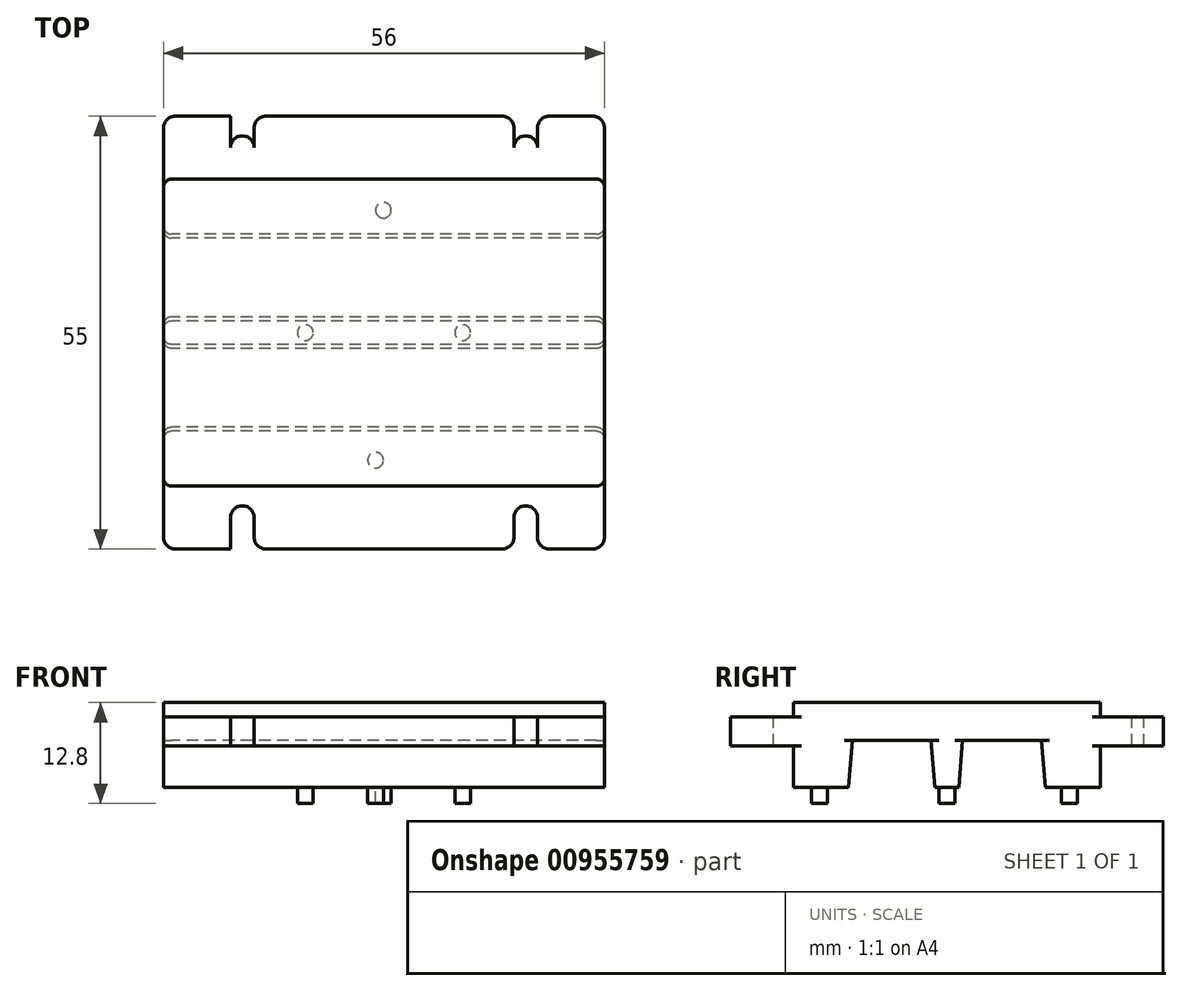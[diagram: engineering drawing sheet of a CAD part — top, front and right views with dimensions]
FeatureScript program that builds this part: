
annotation { "Feature Type Name" : "Feature", "Feature Type Description" : "" }
export const myFeature = defineFeature(function(context is Context, id is Id, definition is map)
    precondition{}
    {
        {
            var Q0;
            Q0=qCreatedBy(makeId("Right.planeOp"),FACE);
            var sketch = newSketch(context, id + "F0", { "sketchPlane" : qUnion([Q0])});
            skLineSegment(sketch, "E0.bottom", {"start": v(0, 0) * mm, "end": v(19.5, 0) * mm});
            skLineSegment(sketch, "E0.top", {"start": v(0, 9) * mm, "end": v(19.5, 9) * mm});
            skLineSegment(sketch, "E0.left", {"start": v(0, 0) * mm, "end": v(0, 9) * mm});
            skLineSegment(sketch, "E0.right", {"start": v(19.5, 0) * mm, "end": v(19.5, 9) * mm});
            skLineSegment(sketch, "E1.bottom", {"start": v(0, 0) * mm, "end": v(-19.5, 0) * mm});
            skLineSegment(sketch, "E1.top", {"start": v(0, 9) * mm, "end": v(-19.5, 9) * mm});
            skLineSegment(sketch, "E1.right", {"start": v(-19.5, 0) * mm, "end": v(-19.5, 9) * mm});
            skLineSegment(sketch, "E2.bottom", {"start": v(19.5, 9) * mm, "end": v(27.5, 9) * mm});
            skLineSegment(sketch, "E2.top", {"start": v(19.5, 5.3) * mm, "end": v(27.5, 5.3) * mm});
            skLineSegment(sketch, "E2.left", {"start": v(19.5, 9) * mm, "end": v(19.5, 5.3) * mm});
            skLineSegment(sketch, "E2.right", {"start": v(27.5, 9) * mm, "end": v(27.5, 5.3) * mm});
            skLineSegment(sketch, "E3.bottom", {"start": v(-19.5, 9) * mm, "end": v(-27.5, 9) * mm});
            skLineSegment(sketch, "E3.top", {"start": v(-19.5, 5.3) * mm, "end": v(-27.5, 5.3) * mm});
            skLineSegment(sketch, "E3.left", {"start": v(-19.5, 9) * mm, "end": v(-19.5, 5.3) * mm});
            skLineSegment(sketch, "E3.right", {"start": v(-27.5, 9) * mm, "end": v(-27.5, 5.3) * mm});
            skLineSegment(sketch, "E4", {"start": v(0, 0) * mm, "end": v(1.5, 0) * mm});
            skLineSegment(sketch, "E5", {"start": v(1.5, 0) * mm, "end": v(2, 6) * mm});
            skLineSegment(sketch, "E6", {"start": v(2, 6) * mm, "end": v(12, 6) * mm});
            skLineSegment(sketch, "E7", {"start": v(12, 6) * mm, "end": v(12.5, 0) * mm});
            skLineSegment(sketch, "E8.MirrorCS", {"start": v(-1.5, 0) * mm, "end": v(-2, 6) * mm});
            skLineSegment(sketch, "E9.MirrorCS", {"start": v(-2, 6) * mm, "end": v(-12, 6) * mm});
            skLineSegment(sketch, "E10.MirrorCS", {"start": v(-12, 6) * mm, "end": v(-12.5, 0) * mm});
            skSolve(sketch);
        }
        {
            var Q0;
            Q0=makeQuery(id+"F0.imprint","IMPRINT",FACE,{"disambiguationData":[TD([[makeQuery(id+"F0.imprint","IMPRINT",EDGE,{"derivedFrom":sQuery(id+"F0.wireOp",EDGE,"E1.top")}),1.0]])]});
            var Q1;
            Q1=makeQuery(id+"F0.imprint","IMPRINT",FACE,{"disambiguationData":[TD([[makeQuery(id+"F0.imprint","IMPRINT",EDGE,{"derivedFrom":sQuery(id+"F0.wireOp",EDGE,"E3.bottom")}),1.0]])]});
            var Q2;
            Q2=makeQuery(id+"F0.imprint","IMPRINT",FACE,{"disambiguationData":[TD([[makeQuery(id+"F0.imprint","IMPRINT",EDGE,{"derivedFrom":sQuery(id+"F0.wireOp",EDGE,"E0.top")}),-1.0]])]});
            var Q3;
            Q3=makeQuery(id+"F0.imprint","IMPRINT",FACE,{"disambiguationData":[TD([[makeQuery(id+"F0.imprint","IMPRINT",EDGE,{"derivedFrom":sQuery(id+"F0.wireOp",EDGE,"E2.bottom")}),-1.0]])]});
            extrude(context, id + "F1", {"entities" : qUnion([Q0, Q1, Q2, Q3]), "depth" : 56 * mm, "offsetDistance" : 25 * mm});
        }
        {
            var Q0;
            Q0=makeQuery(id+"F1.opExtrude","SWEPT_FACE",FACE,{"disambiguationData":[OSD([sQuery(id+"F0.wireOp",EDGE,"E0.top"),sQuery(id+"F0.wireOp",EDGE,"E1.top"),sQuery(id+"F0.wireOp",EDGE,"E2.bottom"),sQuery(id+"F0.wireOp",EDGE,"E3.bottom")])]});
            var sketch = newSketch(context, id + "F2", { "sketchPlane" : qUnion([Q0])});
            skPoint(sketch, "E11", {"position": v(10, 23.5) * mm});
            skPoint(sketch, "E12", {"position": v(46, 23.5) * mm});
            skPoint(sketch, "E13", {"position": v(46, -23.5) * mm});
            skPoint(sketch, "E14", {"position": v(10, -23.5) * mm});
            skCircle(sketch, "E15", {"center": v(10, -23.5) * mm, "radius": 1.5 * mm});
            skCircle(sketch, "E16", {"center": v(46, -23.5) * mm, "radius": 1.5 * mm});
            skLineSegment(sketch, "E17", {"start": v(11.5, -23.5) * mm, "end": v(11.5, -27.5) * mm});
            skLineSegment(sketch, "E18", {"start": v(8.5, -23.5) * mm, "end": v(8.5, -27.5) * mm});
            skLineSegment(sketch, "E19", {"start": v(47.5, -23.5) * mm, "end": v(47.5, -27.5) * mm});
            skLineSegment(sketch, "E20", {"start": v(44.5, -23.5) * mm, "end": v(44.5, -27.5) * mm});
            skLineSegment(sketch, "E21", {"start": v(0, 0) * mm, "end": v(56, 0) * mm});
            skLineSegment(sketch, "E22.MirrorCS", {"start": v(8.5, 23.5) * mm, "end": v(8.5, 27.5) * mm});
            skCircle(sketch, "E23.MirrorC", {"center": v(10, 23.5) * mm, "radius": 1.5 * mm});
            skLineSegment(sketch, "E24.MirrorCS", {"start": v(11.5, 23.5) * mm, "end": v(11.5, 27.5) * mm});
            skCircle(sketch, "E25.MirrorC", {"center": v(46, 23.5) * mm, "radius": 1.5 * mm});
            skLineSegment(sketch, "E26.MirrorCS", {"start": v(44.5, 23.5) * mm, "end": v(44.5, 27.5) * mm});
            skLineSegment(sketch, "E27.MirrorCS", {"start": v(47.5, 23.5) * mm, "end": v(47.5, 27.5) * mm});
            skSolve(sketch);
        }
        {
            var Q0;
            Q0=makeQuery(id+"F1.opExtrude","SWEPT_FACE",FACE,{"disambiguationData":[OSD([sQuery(id+"F0.wireOp",EDGE,"E0.top"),sQuery(id+"F0.wireOp",EDGE,"E1.top"),sQuery(id+"F0.wireOp",EDGE,"E2.bottom"),sQuery(id+"F0.wireOp",EDGE,"E3.bottom")])]});
            var sketch = newSketch(context, id + "F3", { "sketchPlane" : qUnion([Q0])});
            skLineSegment(sketch, "E28.bottom", {"start": v(0, 19.5) * mm, "end": v(56, 19.5) * mm});
            skLineSegment(sketch, "E28.top", {"start": v(0, -19.5) * mm, "end": v(56, -19.5) * mm});
            skLineSegment(sketch, "E28.left", {"start": v(0, 19.5) * mm, "end": v(0, -19.5) * mm});
            skLineSegment(sketch, "E28.right", {"start": v(56, 19.5) * mm, "end": v(56, -19.5) * mm});
            skSolve(sketch);
        }
        {
            var Q0;
            Q0=makeQuery(id+"F3.imprint","IMPRINT",FACE,{"disambiguationData":[TD([[makeQuery(id+"F3.imprint","IMPRINT",EDGE,{"derivedFrom":sQuery(id+"F3.wireOp",EDGE,"E28.bottom")}),-1.0]])]});
            extrude(context, id + "F4", {"entities" : qUnion([Q0]), "operationType" : NewBodyOperationType.ADD, "depth" : 1.8 * mm, "offsetDistance" : 25 * mm});
        }
        {
            var Q0;
            {var subQ0=sQuery(id+"F2.wireOp",EDGE,"E17");Q0=makeQuery(id+"F2.imprint","IMPRINT",FACE,{"disambiguationData":[TD([[makeQuery(id+"F2.imprint","IMPRINT",EDGE,{"derivedFrom":subQ0}),-1.0]])]});}
            var Q1;
            {var subQ0=sQuery(id+"F2.wireOp",EDGE,"E15");var subQ1=makeQuery(id+"F2.imprint","INTERSECT",VERTEX,{"derivedFrom":[subQ0,sQuery(id+"F2.wireOp",EDGE,"E17")]});Q1=makeQuery(id+"F2.imprint","IMPRINT",FACE,{"disambiguationData":[TD([[makeQuery(id+"F2.imprint","IMPRINT",EDGE,{"disambiguationData":[TD([[subQ1,-1.0]])],"derivedFrom":subQ0}),1.0]])]});}
            var Q2;
            {var subQ0=sQuery(id+"F2.wireOp",EDGE,"E19");Q2=makeQuery(id+"F2.imprint","IMPRINT",FACE,{"disambiguationData":[TD([[makeQuery(id+"F2.imprint","IMPRINT",EDGE,{"derivedFrom":subQ0}),-1.0]])]});}
            var Q3;
            {var subQ0=sQuery(id+"F2.wireOp",EDGE,"E16");var subQ1=makeQuery(id+"F2.imprint","INTERSECT",VERTEX,{"derivedFrom":[subQ0,sQuery(id+"F2.wireOp",EDGE,"E19")]});Q3=makeQuery(id+"F2.imprint","IMPRINT",FACE,{"disambiguationData":[TD([[makeQuery(id+"F2.imprint","IMPRINT",EDGE,{"disambiguationData":[TD([[subQ1,-1.0]])],"derivedFrom":subQ0}),1.0]])]});}
            var Q4;
            {var subQ0=sQuery(id+"F2.wireOp",EDGE,"E22.MirrorCS");Q4=makeQuery(id+"F2.imprint","IMPRINT",FACE,{"disambiguationData":[TD([[makeQuery(id+"F2.imprint","IMPRINT",EDGE,{"derivedFrom":subQ0}),-1.0]])]});}
            var Q5;
            {var subQ0=sQuery(id+"F2.wireOp",EDGE,"E23.MirrorC");var subQ1=makeQuery(id+"F2.imprint","INTERSECT",VERTEX,{"derivedFrom":[sQuery(id+"F2.wireOp",EDGE,"E22.MirrorCS"),subQ0]});Q5=makeQuery(id+"F2.imprint","IMPRINT",FACE,{"disambiguationData":[TD([[makeQuery(id+"F2.imprint","IMPRINT",EDGE,{"disambiguationData":[TD([[subQ1,1.0]])],"derivedFrom":subQ0}),-1.0]])]});}
            var Q6;
            {var subQ0=sQuery(id+"F2.wireOp",EDGE,"E25.MirrorC");var subQ1=makeQuery(id+"F2.imprint","INTERSECT",VERTEX,{"derivedFrom":[subQ0,sQuery(id+"F2.wireOp",EDGE,"E26.MirrorCS")]});Q6=makeQuery(id+"F2.imprint","IMPRINT",FACE,{"disambiguationData":[TD([[makeQuery(id+"F2.imprint","IMPRINT",EDGE,{"disambiguationData":[TD([[subQ1,1.0]])],"derivedFrom":subQ0}),-1.0]])]});}
            var Q7;
            {var subQ0=sQuery(id+"F2.wireOp",EDGE,"E26.MirrorCS");Q7=makeQuery(id+"F2.imprint","IMPRINT",FACE,{"disambiguationData":[TD([[makeQuery(id+"F2.imprint","IMPRINT",EDGE,{"derivedFrom":subQ0}),-1.0]])]});}
            extrude(context, id + "F5", {"entities" : qUnion([Q0, Q1, Q2, Q3, Q4, Q5, Q6, Q7]), "operationType" : NewBodyOperationType.REMOVE, "oppositeDirection" : true, "depth" : 25 * mm, "offsetDistance" : 25 * mm});
        }
        {
            var Q0;
            Q0=makeQuery(id+"F1.opExtrude","CAP_EDGE",EDGE,{"disambiguationData":[OSD([sQuery(id+"F0.wireOp",EDGE,"E0.right")])],"isStart":false});
            var Q1;
            Q1=makeQuery(id+"F1.opExtrude","CAP_EDGE",EDGE,{"disambiguationData":[OSD([sQuery(id+"F0.wireOp",EDGE,"E7")])],"isStart":false});
            var Q2;
            Q2=makeQuery(id+"F1.opExtrude","CAP_EDGE",EDGE,{"disambiguationData":[OSD([sQuery(id+"F0.wireOp",EDGE,"E5")])],"isStart":false});
            var Q3;
            Q3=makeQuery(id+"F1.opExtrude","CAP_EDGE",EDGE,{"disambiguationData":[OSD([sQuery(id+"F0.wireOp",EDGE,"E8.MirrorCS")])],"isStart":false});
            var Q4;
            Q4=makeQuery(id+"F1.opExtrude","CAP_EDGE",EDGE,{"disambiguationData":[OSD([sQuery(id+"F0.wireOp",EDGE,"E10.MirrorCS")])],"isStart":false});
            var Q5;
            Q5=makeQuery(id+"F1.opExtrude","CAP_EDGE",EDGE,{"disambiguationData":[OSD([sQuery(id+"F0.wireOp",EDGE,"E1.right")])],"isStart":false});
            var Q6;
            Q6=makeQuery(id+"F4.opExtrude","SWEPT_EDGE",EDGE,{"disambiguationData":[OSD([sQuery(id+"F0.wireOp",EDGE,"E0.top"),sQuery(id+"F0.wireOp",EDGE,"E1.top"),sQuery(id+"F0.wireOp",EDGE,"E2.bottom"),sQuery(id+"F0.wireOp",EDGE,"E3.bottom"),sQuery(id+"F3.wireOp",EDGE,"E28.bottom"),sQuery(id+"F3.wireOp",EDGE,"E28.right")])]});
            var Q7;
            Q7=makeQuery(id+"F4.opExtrude","SWEPT_EDGE",EDGE,{"disambiguationData":[OSD([sQuery(id+"F0.wireOp",EDGE,"E0.top"),sQuery(id+"F0.wireOp",EDGE,"E1.top"),sQuery(id+"F0.wireOp",EDGE,"E2.bottom"),sQuery(id+"F0.wireOp",EDGE,"E3.bottom"),sQuery(id+"F3.wireOp",EDGE,"E28.top"),sQuery(id+"F3.wireOp",EDGE,"E28.right")])]});
            var Q8;
            Q8=makeQuery(id+"F1.opExtrude","CAP_EDGE",EDGE,{"disambiguationData":[OSD([sQuery(id+"F0.wireOp",EDGE,"E0.right")])],"isStart":true});
            var Q9;
            Q9=makeQuery(id+"F1.opExtrude","CAP_EDGE",EDGE,{"disambiguationData":[OSD([sQuery(id+"F0.wireOp",EDGE,"E7")])],"isStart":true});
            var Q10;
            Q10=makeQuery(id+"F1.opExtrude","CAP_EDGE",EDGE,{"disambiguationData":[OSD([sQuery(id+"F0.wireOp",EDGE,"E5")])],"isStart":true});
            var Q11;
            Q11=makeQuery(id+"F1.opExtrude","CAP_EDGE",EDGE,{"disambiguationData":[OSD([sQuery(id+"F0.wireOp",EDGE,"E8.MirrorCS")])],"isStart":true});
            var Q12;
            Q12=makeQuery(id+"F4.opExtrude","SWEPT_EDGE",EDGE,{"disambiguationData":[OSD([sQuery(id+"F0.wireOp",EDGE,"E0.top"),sQuery(id+"F0.wireOp",EDGE,"E1.top"),sQuery(id+"F0.wireOp",EDGE,"E2.bottom"),sQuery(id+"F0.wireOp",EDGE,"E3.bottom"),sQuery(id+"F3.wireOp",EDGE,"E28.bottom"),sQuery(id+"F3.wireOp",EDGE,"E28.left")])]});
            var Q13;
            Q13=makeQuery(id+"F1.opExtrude","CAP_EDGE",EDGE,{"disambiguationData":[OSD([sQuery(id+"F0.wireOp",EDGE,"E10.MirrorCS")])],"isStart":true});
            var Q14;
            Q14=makeQuery(id+"F1.opExtrude","CAP_EDGE",EDGE,{"disambiguationData":[OSD([sQuery(id+"F0.wireOp",EDGE,"E1.right")])],"isStart":true});
            var Q15;
            Q15=makeQuery(id+"F4.opExtrude","SWEPT_EDGE",EDGE,{"disambiguationData":[OSD([sQuery(id+"F0.wireOp",EDGE,"E0.top"),sQuery(id+"F0.wireOp",EDGE,"E1.top"),sQuery(id+"F0.wireOp",EDGE,"E2.bottom"),sQuery(id+"F0.wireOp",EDGE,"E3.bottom"),sQuery(id+"F3.wireOp",EDGE,"E28.top"),sQuery(id+"F3.wireOp",EDGE,"E28.left")])]});
            fillet(context, id + "F6", {"entities" : qUnion([Q0, Q1, Q2, Q3, Q4, Q5, Q6, Q7, Q8, Q9, Q10, Q11, Q12, Q13, Q14, Q15]), "radius" : 1 * mm, "tangentPropagation" : true, "allowEdgeOverflow" : false});
        }
        {
            var Q0;
            Q0=makeQuery(id+"F1.opExtrude","CAP_EDGE",EDGE,{"disambiguationData":[OSD([sQuery(id+"F0.wireOp",EDGE,"E3.right")])],"isStart":true});
            var Q1;
            Q1=makeQuery(id+"F5.boolean.opBoolean","COPY",EDGE,{"derivedFrom":makeQuery(id+"F5.opExtrude","SWEPT_EDGE",EDGE,{"disambiguationData":[OSD([sQuery(id+"F0.wireOp",EDGE,"E3.bottom"),sQuery(id+"F0.wireOp",EDGE,"E3.right"),sQuery(id+"F2.wireOp",EDGE,"E18")])]})});
            var Q2;
            Q2=makeQuery(id+"F5.boolean.opBoolean","COPY",EDGE,{"derivedFrom":makeQuery(id+"F5.opExtrude","SWEPT_EDGE",EDGE,{"disambiguationData":[OSD([sQuery(id+"F0.wireOp",EDGE,"E3.bottom"),sQuery(id+"F0.wireOp",EDGE,"E3.right"),sQuery(id+"F2.wireOp",EDGE,"E17")])]})});
            var Q3;
            Q3=makeQuery(id+"F5.boolean.opBoolean","COPY",EDGE,{"derivedFrom":makeQuery(id+"F5.opExtrude","SWEPT_EDGE",EDGE,{"disambiguationData":[OSD([sQuery(id+"F0.wireOp",EDGE,"E3.bottom"),sQuery(id+"F0.wireOp",EDGE,"E3.right"),sQuery(id+"F2.wireOp",EDGE,"E19")])]})});
            var Q4;
            Q4=makeQuery(id+"F5.boolean.opBoolean","COPY",EDGE,{"derivedFrom":makeQuery(id+"F5.opExtrude","SWEPT_EDGE",EDGE,{"disambiguationData":[OSD([sQuery(id+"F0.wireOp",EDGE,"E3.bottom"),sQuery(id+"F0.wireOp",EDGE,"E3.right"),sQuery(id+"F2.wireOp",EDGE,"E20")])]})});
            var Q5;
            Q5=makeQuery(id+"F1.opExtrude","CAP_EDGE",EDGE,{"disambiguationData":[OSD([sQuery(id+"F0.wireOp",EDGE,"E3.right")])],"isStart":false});
            var Q6;
            Q6=makeQuery(id+"F1.opExtrude","CAP_EDGE",EDGE,{"disambiguationData":[OSD([sQuery(id+"F0.wireOp",EDGE,"E2.right")])],"isStart":true});
            var Q7;
            Q7=makeQuery(id+"F5.boolean.opBoolean","COPY",EDGE,{"derivedFrom":makeQuery(id+"F5.opExtrude","SWEPT_EDGE",EDGE,{"disambiguationData":[OSD([sQuery(id+"F0.wireOp",EDGE,"E2.bottom"),sQuery(id+"F0.wireOp",EDGE,"E2.right"),sQuery(id+"F2.wireOp",EDGE,"E22.MirrorCS")])]})});
            var Q8;
            Q8=makeQuery(id+"F5.boolean.opBoolean","COPY",EDGE,{"derivedFrom":makeQuery(id+"F5.opExtrude","SWEPT_EDGE",EDGE,{"disambiguationData":[OSD([sQuery(id+"F0.wireOp",EDGE,"E2.bottom"),sQuery(id+"F0.wireOp",EDGE,"E2.right"),sQuery(id+"F2.wireOp",EDGE,"E24.MirrorCS")])]})});
            var Q9;
            Q9=makeQuery(id+"F5.boolean.opBoolean","COPY",EDGE,{"derivedFrom":makeQuery(id+"F5.opExtrude","SWEPT_EDGE",EDGE,{"disambiguationData":[OSD([sQuery(id+"F0.wireOp",EDGE,"E2.bottom"),sQuery(id+"F0.wireOp",EDGE,"E2.right"),sQuery(id+"F2.wireOp",EDGE,"E26.MirrorCS")])]})});
            var Q10;
            Q10=makeQuery(id+"F5.boolean.opBoolean","COPY",EDGE,{"derivedFrom":makeQuery(id+"F5.opExtrude","SWEPT_EDGE",EDGE,{"disambiguationData":[OSD([sQuery(id+"F0.wireOp",EDGE,"E2.bottom"),sQuery(id+"F0.wireOp",EDGE,"E2.right"),sQuery(id+"F2.wireOp",EDGE,"E27.MirrorCS")])]})});
            var Q11;
            Q11=makeQuery(id+"F1.opExtrude","CAP_EDGE",EDGE,{"disambiguationData":[OSD([sQuery(id+"F0.wireOp",EDGE,"E2.right")])],"isStart":false});
            fillet(context, id + "F7", {"entities" : qUnion([Q0, Q1, Q2, Q3, Q4, Q5, Q6, Q7, Q8, Q9, Q10, Q11]), "radius" : 1.5 * mm, "tangentPropagation" : true, "allowEdgeOverflow" : false});
        }
        {
            var Q0;
            Q0=makeQuery(id+"F1.opExtrude","SWEPT_FACE",FACE,{"disambiguationData":[OSD([sQuery(id+"F0.wireOp",EDGE,"E1.bottom")])]});
            var sketch = newSketch(context, id + "F8", { "sketchPlane" : qUnion([Q0])});
            skCircle(sketch, "E29", {"center": v(6.92, 16.07) * mm, "radius": 1 * mm});
            skCircle(sketch, "E30", {"center": v(26.92, 16.2) * mm, "radius": 1 * mm});
            skCircle(sketch, "E31", {"center": v(46.92, 16.07) * mm, "radius": 1 * mm});
            skCircle(sketch, "E32", {"center": v(7.92, -15.55) * mm, "radius": 1 * mm});
            skCircle(sketch, "E33", {"center": v(27.92, -15.55) * mm, "radius": 1 * mm});
            skCircle(sketch, "E34", {"center": v(47.92, -15.55) * mm, "radius": 1 * mm});
            skCircle(sketch, "E35", {"center": v(18, 0) * mm, "radius": 1 * mm});
            skCircle(sketch, "E36", {"center": v(38, 0) * mm, "radius": 1 * mm});
            skSolve(sketch);
        }
        {
            var Q0;
            Q0=makeQuery(id+"F8.imprint","IMPRINT",FACE,{"disambiguationData":[TD([[makeQuery(id+"F8.imprint","IMPRINT",EDGE,{"derivedFrom":sQuery(id+"F8.wireOp",EDGE,"E36")}),1.0]])]});
            var Q1;
            Q1=makeQuery(id+"F8.imprint","IMPRINT",FACE,{"disambiguationData":[TD([[makeQuery(id+"F8.imprint","IMPRINT",EDGE,{"derivedFrom":sQuery(id+"F8.wireOp",EDGE,"E35")}),1.0]])]});
            var Q2;
            Q2=makeQuery(id+"F8.imprint","IMPRINT",FACE,{"disambiguationData":[TD([[makeQuery(id+"F8.imprint","IMPRINT",EDGE,{"derivedFrom":sQuery(id+"F8.wireOp",EDGE,"E30")}),1.0]])]});
            var Q3;
            Q3=makeQuery(id+"F8.imprint","IMPRINT",FACE,{"disambiguationData":[TD([[makeQuery(id+"F8.imprint","IMPRINT",EDGE,{"derivedFrom":sQuery(id+"F8.wireOp",EDGE,"E33")}),1.0]])]});
            extrude(context, id + "F9", {"entities" : qUnion([Q0, Q1, Q2, Q3]), "operationType" : NewBodyOperationType.ADD, "depth" : 2 * mm, "offsetDistance" : 25 * mm});
        }
    });
